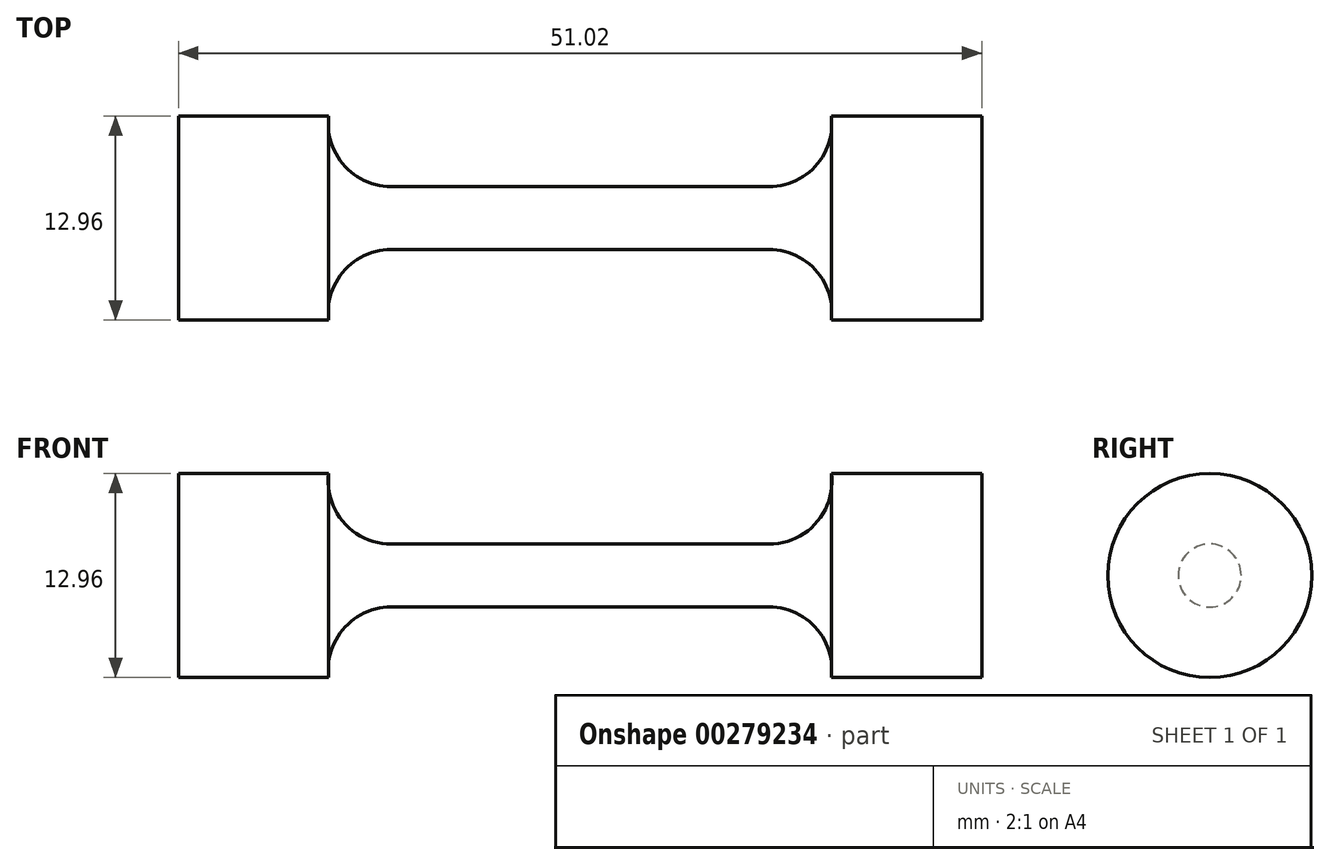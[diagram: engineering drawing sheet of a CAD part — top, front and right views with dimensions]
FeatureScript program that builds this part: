
annotation { "Feature Type Name" : "Feature", "Feature Type Description" : "" }
export const myFeature = defineFeature(function(context is Context, id is Id, definition is map)
    precondition{}
    {
        {
            var Q0;
            Q0=qCreatedBy(makeId("Front.planeOp"),FACE);
            var sketch = newSketch(context, id + "F0", { "sketchPlane" : qUnion([Q0])});
            skLineSegment(sketch, "E0", {"start": v(0, 2) * mm, "end": v(12, 2) * mm});
            skArc(sketch, "E1", {"start": v(12, 2) * mm, "mid": v(15, 3.35) * mm, "end": v(15.97, 6.48) * mm});
            skLineSegment(sketch, "E2", {"start": v(15.97, 6.48) * mm, "end": v(25.51, 6.48) * mm});
            skLineSegment(sketch, "E3", {"start": v(25.51, 6.48) * mm, "end": v(25.51, 0) * mm});
            skLineSegment(sketch, "E4.MirrorCS", {"start": v(0, 2) * mm, "end": v(-12, 2) * mm});
            skLineSegment(sketch, "E5.MirrorCS", {"start": v(-25.51, 6.48) * mm, "end": v(-25.51, 0) * mm});
            skLineSegment(sketch, "E6.MirrorCS", {"start": v(-15.97, 6.48) * mm, "end": v(-25.51, 6.48) * mm});
            skArc(sketch, "E7.MirrorCS", {"start": v(-12, 2) * mm, "mid": v(-15, 3.35) * mm, "end": v(-15.97, 6.48) * mm});
            skLineSegment(sketch, "E8", {"start": v(-25.51, 0) * mm, "end": v(25.51, 0) * mm});
            skSolve(sketch);
        }
        {
            var Q0;
            Q0=makeQuery(id+"F0.imprint","IMPRINT",FACE,{"disambiguationData":[TD([[makeQuery(id+"F0.imprint","IMPRINT",EDGE,{"derivedFrom":sQuery(id+"F0.wireOp",EDGE,"E0")}),-1.0]])]});
            var Q1;
            Q1=sQuery(id+"F0.wireOp",EDGE,"E8");
            revolve(context, id + "F1", {"entities" : qUnion([Q0]), "axis" : qUnion([Q1]), "revolveType" : RevolveType.FULL});
        }
    });
